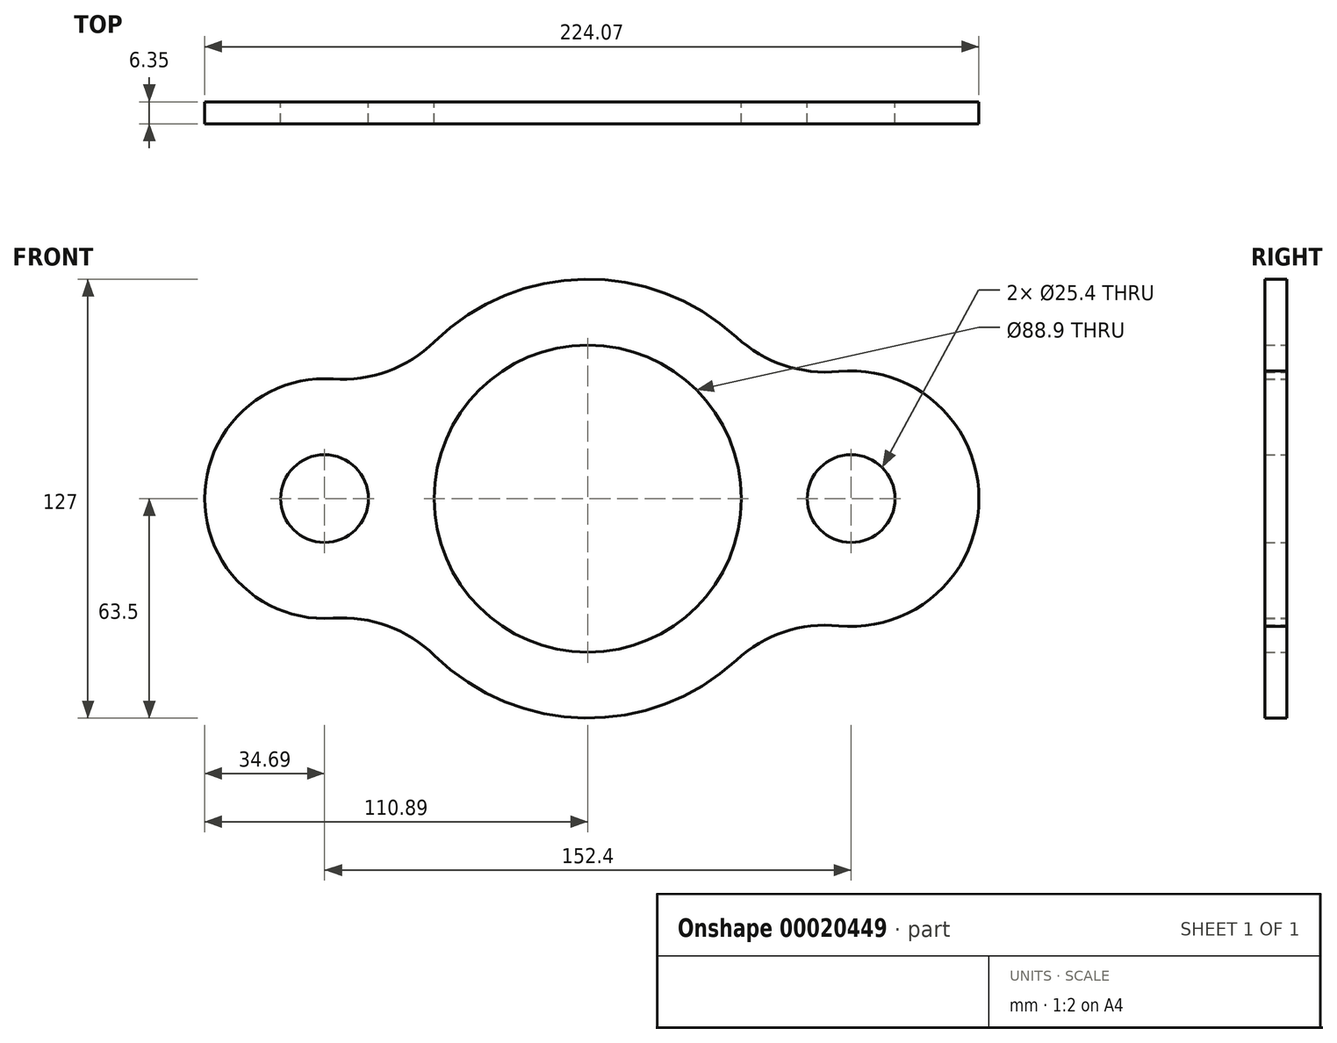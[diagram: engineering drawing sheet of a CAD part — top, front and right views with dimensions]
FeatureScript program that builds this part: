
annotation { "Feature Type Name" : "Feature", "Feature Type Description" : "" }
export const myFeature = defineFeature(function(context is Context, id is Id, definition is map)
    precondition{}
    {
        {
            var Q0;
            Q0=qCreatedBy(makeId("Front.planeOp"),FACE);
            var sketch = newSketch(context, id + "F0", { "sketchPlane" : qUnion([Q0])});
            skCircle(sketch, "E0", {"center": v(0, 0) * mm, "radius": 44.45 * mm});
            skCircle(sketch, "E1", {"center": v(-76.2, 0) * mm, "radius": 12.7 * mm});
            skCircle(sketch, "E2", {"center": v(76.2, 0) * mm, "radius": 12.7 * mm});
            skArc(sketch, "E3", {"start": v(43.03, 46.7) * mm, "mid": v(-0.96, 63.5) * mm, "end": v(-44.41, 45.38) * mm});
            skArc(sketch, "E4", {"start": v(-73.75, 34.6) * mm, "mid": v(-110.9, 0) * mm, "end": v(-73.75, -34.6) * mm});
            skArc(sketch, "E5", {"start": v(72.58, -36.8) * mm, "mid": v(113.18, 0) * mm, "end": v(72.58, 36.8) * mm});
            skArc(sketch, "E6.trimOffspring", {"start": v(-44.41, -45.38) * mm, "mid": v(-0.96, -63.5) * mm, "end": v(43.03, -46.7) * mm});
            skPoint(sketch, "E7.visualSharp", {"position": v(-56.66, 28.67) * mm});
            skArc(sketch, "E7.filletArc", {"start": v(-73.75, 34.6) * mm, "mid": v(-57.93, 36.85) * mm, "end": v(-44.41, 45.38) * mm});
            skPoint(sketch, "E8.visualSharp", {"position": v(-56.66, -28.67) * mm});
            skArc(sketch, "E8.filletArc", {"start": v(-44.41, -45.38) * mm, "mid": v(-57.93, -36.85) * mm, "end": v(-73.75, -34.6) * mm});
            skPoint(sketch, "E9.visualSharp", {"position": v(55.59, 30.7) * mm});
            skArc(sketch, "E9.filletArc", {"start": v(43.03, 46.7) * mm, "mid": v(56.74, 38.6) * mm, "end": v(72.58, 36.8) * mm});
            skPoint(sketch, "E10.visualSharp", {"position": v(55.59, -30.7) * mm});
            skArc(sketch, "E10.filletArc", {"start": v(72.58, -36.8) * mm, "mid": v(56.74, -38.6) * mm, "end": v(43.03, -46.7) * mm});
            skSolve(sketch);
        }
        {
            var Q0;
            Q0=makeQuery(id+"F0.imprint","IMPRINT",FACE,{"disambiguationData":[TD([[makeQuery(id+"F0.imprint","IMPRINT",EDGE,{"derivedFrom":sQuery(id+"F0.wireOp",EDGE,"E0")}),-1.0]])]});
            extrude(context, id + "F1", {"entities" : qUnion([Q0]), "depth" : 6.35 * mm});
        }
    });
